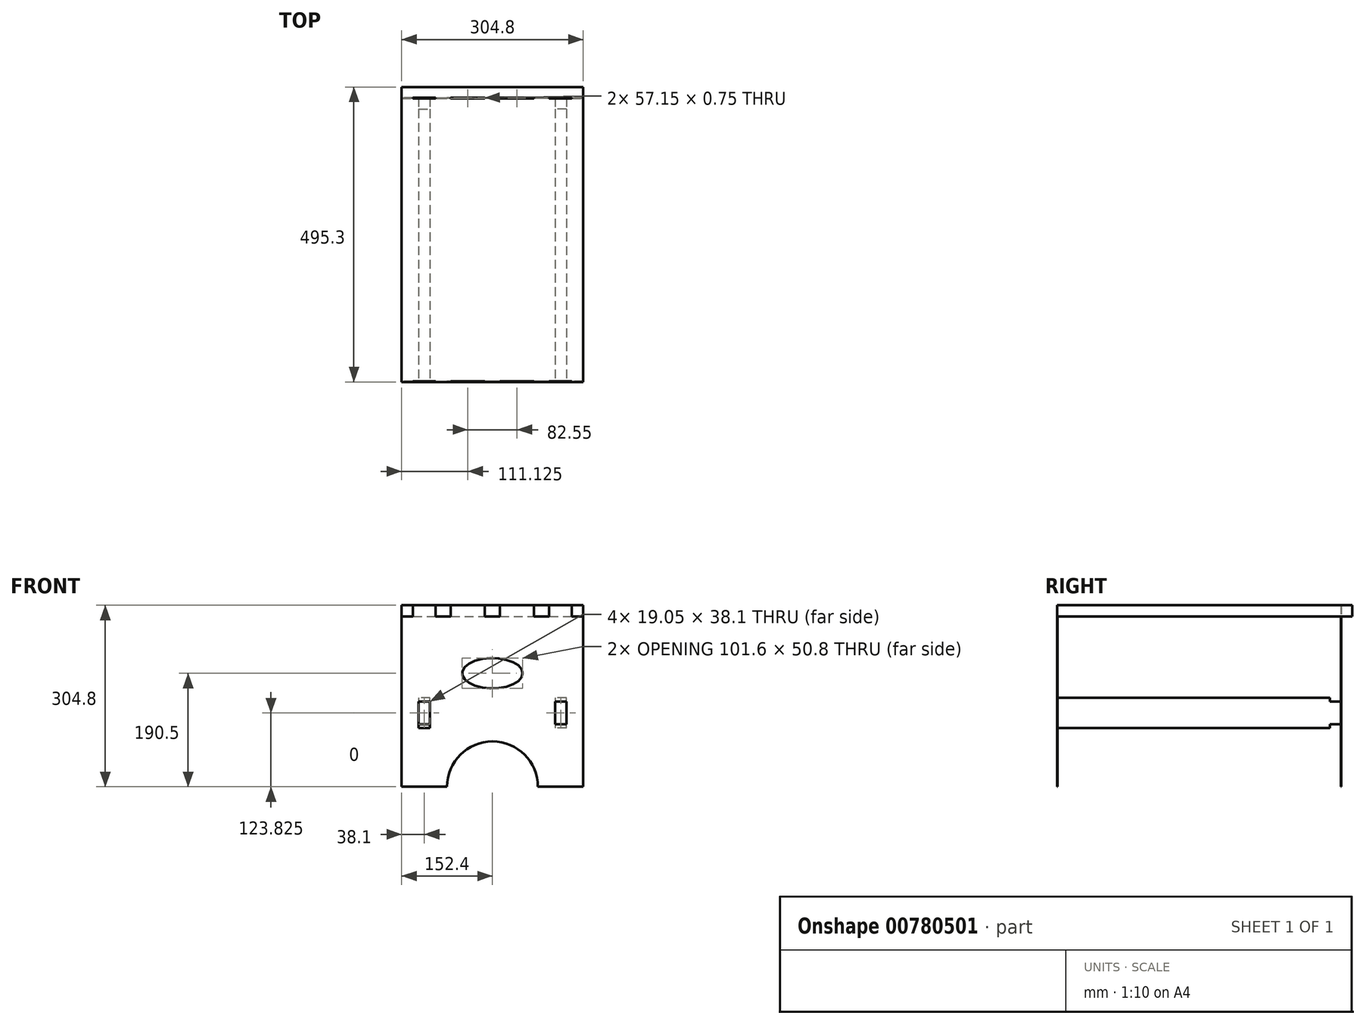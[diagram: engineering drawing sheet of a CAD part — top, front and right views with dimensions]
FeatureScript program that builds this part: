
annotation { "Feature Type Name" : "Feature", "Feature Type Description" : "" }
export const myFeature = defineFeature(function(context is Context, id is Id, definition is map)
    precondition{}
    {
        {
            assignVariable(context, id + "F0", {"name" : "PLY", "anyValue" : 0.75});
        }
        {
            var Q0;
            Q0=qCreatedBy(makeId("Front.planeOp"),FACE);
            var sketch = newSketch(context, id + "F1", { "sketchPlane" : qUnion([Q0])});
            skLineSegment(sketch, "E0", {"start": v(0, 0) * mm, "end": v(76.2, 0) * mm});
            skLineSegment(sketch, "E1", {"start": v(0, 0) * mm, "end": v(0, 304.8) * mm});
            skLineSegment(sketch, "E2", {"start": v(0, 304.8) * mm, "end": v(139.7, 304.8) * mm});
            skLineSegment(sketch, "E3", {"start": v(304.8, 304.8) * mm, "end": v(304.8, 0) * mm});
            skLineSegment(sketch, "E4", {"start": v(304.8, 0) * mm, "end": v(228.6, 0) * mm});
            skLineSegment(sketch, "E5", {"start": v(228.6, 0) * mm, "end": v(228.6, 76.2) * mm});
            skLineSegment(sketch, "E6", {"start": v(76.2, 0) * mm, "end": v(76.2, 76.2) * mm});
            skLineSegment(sketch, "E7", {"start": v(76.2, 76.2) * mm, "end": v(228.6, 76.2) * mm});
            skLineSegment(sketch, "E8", {"start": v(152.4, 304.8) * mm, "end": v(152.4, 76.2) * mm});
            skEllipse(sketch, "E9", {"center": v(152.4, 190.5) * mm, "majorRadius": 50.8 * mm, "minorRadius": 25.4 * mm, "majorAxis": v(1, 0)});
            skLineSegment(sketch, "E10", {"start": v(0, 304.8) * mm, "end": v(19.05, 304.8) * mm});
            skLineSegment(sketch, "E11", {"start": v(19.05, 304.8) * mm, "end": v(19.05, 285.75) * mm});
            skLineSegment(sketch, "E12", {"start": v(19.05, 285.75) * mm, "end": v(0, 285.75) * mm});
            skLineSegment(sketch, "E13", {"start": v(304.8, 304.8) * mm, "end": v(285.75, 304.8) * mm});
            skLineSegment(sketch, "E14", {"start": v(285.75, 304.8) * mm, "end": v(285.75, 285.75) * mm});
            skLineSegment(sketch, "E15", {"start": v(285.75, 285.75) * mm, "end": v(304.8, 285.75) * mm});
            skLineSegment(sketch, "E16", {"start": v(19.05, 304.8) * mm, "end": v(57.15, 304.8) * mm});
            skLineSegment(sketch, "E17", {"start": v(57.15, 304.8) * mm, "end": v(57.15, 285.75) * mm});
            skLineSegment(sketch, "E18", {"start": v(57.15, 285.75) * mm, "end": v(82.55, 285.75) * mm});
            skLineSegment(sketch, "E19", {"start": v(82.55, 285.75) * mm, "end": v(82.55, 304.8) * mm});
            skLineSegment(sketch, "E20", {"start": v(285.75, 304.8) * mm, "end": v(247.65, 304.8) * mm});
            skLineSegment(sketch, "E21", {"start": v(247.65, 304.8) * mm, "end": v(247.65, 285.75) * mm});
            skLineSegment(sketch, "E22", {"start": v(247.65, 285.75) * mm, "end": v(222.25, 285.75) * mm});
            skLineSegment(sketch, "E23", {"start": v(222.25, 285.75) * mm, "end": v(222.25, 304.8) * mm});
            skLineSegment(sketch, "E24", {"start": v(165.1, 304.8) * mm, "end": v(165.1, 285.75) * mm});
            skLineSegment(sketch, "E25", {"start": v(165.1, 285.75) * mm, "end": v(152.4, 285.75) * mm});
            skLineSegment(sketch, "E26", {"start": v(152.4, 285.75) * mm, "end": v(139.7, 285.75) * mm});
            skLineSegment(sketch, "E27", {"start": v(139.7, 285.75) * mm, "end": v(139.7, 304.8) * mm});
            skLineSegment(sketch, "E28.trimOffspring", {"start": v(165.1, 304.8) * mm, "end": v(304.8, 304.8) * mm});
            skLineSegment(sketch, "E29", {"start": v(266.7, 0) * mm, "end": v(266.7, 101.6) * mm});
            skLineSegment(sketch, "E30.top", {"start": v(273.94, 104.78) * mm, "end": v(261.24, 104.78) * mm});
            skLineSegment(sketch, "E30.right", {"start": v(261.24, 123.83) * mm, "end": v(261.24, 123.82) * mm});
            skLineSegment(sketch, "E31", {"start": v(266.7, 101.6) * mm, "end": v(266.7, 104.78) * mm});
            skLineSegment(sketch, "E32", {"start": v(38.1, 0) * mm, "end": v(38.1, 104.78) * mm});
            skLineSegment(sketch, "E33", {"start": v(38.1, 104.78) * mm, "end": v(44.45, 104.78) * mm});
            skLineSegment(sketch, "E34.bottom", {"start": v(38.1, 104.78) * mm, "end": v(31.75, 104.78) * mm});
            skPoint(sketch, "E35.end.orphan", {"position": v(261.24, 123.82) * mm});
            skLineSegment(sketch, "E36", {"start": v(261.24, 104.78) * mm, "end": v(258.07, 104.78) * mm});
            skLineSegment(sketch, "E37.bottom", {"start": v(276.7, 104.78) * mm, "end": v(257.64, 104.78) * mm});
            skLineSegment(sketch, "E38", {"start": v(44.45, 104.78) * mm, "end": v(47.62, 104.78) * mm});
            skLineSegment(sketch, "E39.bottom", {"start": v(47.62, 104.78) * mm, "end": v(28.57, 104.78) * mm});
            skLineSegment(sketch, "E40.top", {"start": v(47.62, 142.88) * mm, "end": v(28.57, 142.88) * mm});
            skLineSegment(sketch, "E40.left", {"start": v(47.62, 104.78) * mm, "end": v(47.62, 142.88) * mm});
            skLineSegment(sketch, "E40.right", {"start": v(28.57, 104.78) * mm, "end": v(28.57, 142.88) * mm});
            skLineSegment(sketch, "E41.top", {"start": v(276.7, 142.88) * mm, "end": v(257.64, 142.88) * mm});
            skLineSegment(sketch, "E41.left", {"start": v(276.7, 104.78) * mm, "end": v(276.7, 142.88) * mm});
            skLineSegment(sketch, "E41.right", {"start": v(257.64, 104.78) * mm, "end": v(257.64, 142.88) * mm});
            skSolve(sketch);
        }
        {
            var Q0;
            {var subQ12=sQuery(id+"F1.wireOp",EDGE,"E4");Q0=makeQuery(id+"F1.imprint","IMPRINT",FACE,{"disambiguationData":[TD([[makeQuery(id+"F1.imprint","IMPRINT",EDGE,{"derivedFrom":subQ12}),-1.0]])]});}
            var Q1;
            {var subQ10=sQuery(id+"F1.wireOp",EDGE,"E0");Q1=makeQuery(id+"F1.imprint","IMPRINT",FACE,{"disambiguationData":[TD([[makeQuery(id+"F1.imprint","IMPRINT",EDGE,{"derivedFrom":subQ10}),1.0]])]});}
            extrude(context, id + "F2", {"entities" : qUnion([Q0, Q1]), "depth" : (getVariable(context, 'PLY')) * mm, "offsetDistance" : 25.4 * mm});
        }
        {
            var Q0;
            Q0=makeQuery(id+"F2.opExtrude","SWEPT_EDGE",EDGE,{"disambiguationData":[OSD([sQuery(id+"F1.wireOp",EDGE,"E6"),sQuery(id+"F1.wireOp",EDGE,"E7")])]});
            var Q1;
            Q1=makeQuery(id+"F2.opExtrude","SWEPT_EDGE",EDGE,{"disambiguationData":[OSD([sQuery(id+"F1.wireOp",EDGE,"E5"),sQuery(id+"F1.wireOp",EDGE,"E7")])]});
            fillet(context, id + "F3", {"entities" : qUnion([Q0, Q1]), "radius" : 76.2 * mm, "tangentPropagation" : true, "allowEdgeOverflow" : false});
        }
        {
            var Q0;
            Q0=makeQuery(id+"F2.opExtrude","CAP_FACE",FACE,{"disambiguationData":[OSD([sQuery(id+"F1.wireOp",EDGE,"E0"),sQuery(id+"F1.wireOp",EDGE,"E1"),sQuery(id+"F1.wireOp",EDGE,"E2"),sQuery(id+"F1.wireOp",EDGE,"E3"),sQuery(id+"F1.wireOp",EDGE,"E4"),sQuery(id+"F1.wireOp",EDGE,"E5"),sQuery(id+"F1.wireOp",EDGE,"E6"),sQuery(id+"F1.wireOp",EDGE,"E7"),sQuery(id+"F1.wireOp",EDGE,"E9"),sQuery(id+"F1.wireOp",EDGE,"E11"),sQuery(id+"F1.wireOp",EDGE,"E12"),sQuery(id+"F1.wireOp",EDGE,"E14"),sQuery(id+"F1.wireOp",EDGE,"E15"),sQuery(id+"F1.wireOp",EDGE,"E16"),sQuery(id+"F1.wireOp",EDGE,"E17"),sQuery(id+"F1.wireOp",EDGE,"E18"),sQuery(id+"F1.wireOp",EDGE,"E19"),sQuery(id+"F1.wireOp",EDGE,"E21"),sQuery(id+"F1.wireOp",EDGE,"E22"),sQuery(id+"F1.wireOp",EDGE,"E23"),sQuery(id+"F1.wireOp",EDGE,"E24"),sQuery(id+"F1.wireOp",EDGE,"E25"),sQuery(id+"F1.wireOp",EDGE,"E26"),sQuery(id+"F1.wireOp",EDGE,"E27"),sQuery(id+"F1.wireOp",EDGE,"E28.trimOffspring"),sQuery(id+"F1.wireOp",EDGE,"E37.bottom"),sQuery(id+"F1.wireOp",EDGE,"E37.top"),sQuery(id+"F1.wireOp",EDGE,"E37.left"),sQuery(id+"F1.wireOp",EDGE,"E37.right"),sQuery(id+"F1.wireOp",EDGE,"E39.bottom"),sQuery(id+"F1.wireOp",EDGE,"E39.top"),sQuery(id+"F1.wireOp",EDGE,"E39.left"),sQuery(id+"F1.wireOp",EDGE,"E39.right")])],"isStart":true});
            var sketch = newSketch(context, id + "F4", { "sketchPlane" : qUnion([Q0])});
            skLineSegment(sketch, "E42", {"start": v(-276.7, 142.88) * mm, "end": v(-276.7, 149.23) * mm});
            skLineSegment(sketch, "E43.bottom", {"start": v(-276.7, 149.23) * mm, "end": v(-257.64, 149.23) * mm});
            skLineSegment(sketch, "E43.top", {"start": v(-276.7, 98.43) * mm, "end": v(-257.64, 98.43) * mm});
            skLineSegment(sketch, "E43.left", {"start": v(-276.7, 149.23) * mm, "end": v(-276.7, 98.43) * mm});
            skLineSegment(sketch, "E43.right", {"start": v(-257.64, 149.23) * mm, "end": v(-257.64, 98.43) * mm});
            skLineSegment(sketch, "E44", {"start": v(-47.62, 142.88) * mm, "end": v(-47.62, 149.22) * mm});
            skLineSegment(sketch, "E45.bottom", {"start": v(-47.62, 149.22) * mm, "end": v(-28.57, 149.22) * mm});
            skLineSegment(sketch, "E45.top", {"start": v(-47.62, 98.42) * mm, "end": v(-28.57, 98.42) * mm});
            skLineSegment(sketch, "E45.left", {"start": v(-47.62, 149.22) * mm, "end": v(-47.62, 98.42) * mm});
            skLineSegment(sketch, "E45.right", {"start": v(-28.57, 149.22) * mm, "end": v(-28.57, 98.42) * mm});
            skSolve(sketch);
        }
        {
            var Q0;
            Q0=makeQuery(id+"F2.opExtrude","CAP_FACE",FACE,{"disambiguationData":[OSD([sQuery(id+"F1.wireOp",EDGE,"E0"),sQuery(id+"F1.wireOp",EDGE,"E1"),sQuery(id+"F1.wireOp",EDGE,"E2"),sQuery(id+"F1.wireOp",EDGE,"E3"),sQuery(id+"F1.wireOp",EDGE,"E4"),sQuery(id+"F1.wireOp",EDGE,"E5"),sQuery(id+"F1.wireOp",EDGE,"E6"),sQuery(id+"F1.wireOp",EDGE,"E7"),sQuery(id+"F1.wireOp",EDGE,"E9"),sQuery(id+"F1.wireOp",EDGE,"E11"),sQuery(id+"F1.wireOp",EDGE,"E12"),sQuery(id+"F1.wireOp",EDGE,"E14"),sQuery(id+"F1.wireOp",EDGE,"E15"),sQuery(id+"F1.wireOp",EDGE,"E16"),sQuery(id+"F1.wireOp",EDGE,"E17"),sQuery(id+"F1.wireOp",EDGE,"E18"),sQuery(id+"F1.wireOp",EDGE,"E19"),sQuery(id+"F1.wireOp",EDGE,"E21"),sQuery(id+"F1.wireOp",EDGE,"E22"),sQuery(id+"F1.wireOp",EDGE,"E23"),sQuery(id+"F1.wireOp",EDGE,"E24"),sQuery(id+"F1.wireOp",EDGE,"E25"),sQuery(id+"F1.wireOp",EDGE,"E26"),sQuery(id+"F1.wireOp",EDGE,"E27"),sQuery(id+"F1.wireOp",EDGE,"E28.trimOffspring"),sQuery(id+"F1.wireOp",EDGE,"E37.bottom"),sQuery(id+"F1.wireOp",EDGE,"E37.top"),sQuery(id+"F1.wireOp",EDGE,"E37.left"),sQuery(id+"F1.wireOp",EDGE,"E37.right"),sQuery(id+"F1.wireOp",EDGE,"E39.bottom"),sQuery(id+"F1.wireOp",EDGE,"E39.top"),sQuery(id+"F1.wireOp",EDGE,"E39.left"),sQuery(id+"F1.wireOp",EDGE,"E39.right")])],"isStart":false});
            var sketch = newSketch(context, id + "F5", { "sketchPlane" : qUnion([Q0])});
            skLineSegment(sketch, "E46", {"start": v(0, 285.75) * mm, "end": v(0, 304.8) * mm});
            skLineSegment(sketch, "E47.bottom", {"start": v(0, 304.8) * mm, "end": v(304.8, 304.8) * mm});
            skLineSegment(sketch, "E47.top", {"start": v(0, 285.75) * mm, "end": v(304.8, 285.75) * mm});
            skLineSegment(sketch, "E47.left", {"start": v(0, 304.8) * mm, "end": v(0, 285.75) * mm});
            skLineSegment(sketch, "E47.right", {"start": v(304.8, 304.8) * mm, "end": v(304.8, 285.75) * mm});
            skSolve(sketch);
        }
        {
            var Q0;
            Q0 = qSketchRegion(id + "F5", true);
            extrude(context, id + "F6", {"entities" : qUnion([Q0]), "oppositeDirection" : true, "depth" : 495.3 * mm, "offsetDistance" : 25.4 * mm});
        }
        {
            var Q0;
            Q0=makeQuery(id+"F2.opExtrude","SWEPT_BODY",BODY,{"disambiguationData":[OSD([sQuery(id+"F1.wireOp",EDGE,"E0"),sQuery(id+"F1.wireOp",EDGE,"E1"),sQuery(id+"F1.wireOp",EDGE,"E2"),sQuery(id+"F1.wireOp",EDGE,"E3"),sQuery(id+"F1.wireOp",EDGE,"E4"),sQuery(id+"F1.wireOp",EDGE,"E5"),sQuery(id+"F1.wireOp",EDGE,"E6"),sQuery(id+"F1.wireOp",EDGE,"E7"),sQuery(id+"F1.wireOp",EDGE,"E9"),sQuery(id+"F1.wireOp",EDGE,"E11"),sQuery(id+"F1.wireOp",EDGE,"E12"),sQuery(id+"F1.wireOp",EDGE,"E14"),sQuery(id+"F1.wireOp",EDGE,"E15"),sQuery(id+"F1.wireOp",EDGE,"E16"),sQuery(id+"F1.wireOp",EDGE,"E17"),sQuery(id+"F1.wireOp",EDGE,"E18"),sQuery(id+"F1.wireOp",EDGE,"E19"),sQuery(id+"F1.wireOp",EDGE,"E21"),sQuery(id+"F1.wireOp",EDGE,"E22"),sQuery(id+"F1.wireOp",EDGE,"E23"),sQuery(id+"F1.wireOp",EDGE,"E24"),sQuery(id+"F1.wireOp",EDGE,"E25"),sQuery(id+"F1.wireOp",EDGE,"E26"),sQuery(id+"F1.wireOp",EDGE,"E27"),sQuery(id+"F1.wireOp",EDGE,"E28.trimOffspring"),sQuery(id+"F1.wireOp",EDGE,"E39.bottom"),sQuery(id+"F1.wireOp",EDGE,"E40.top"),sQuery(id+"F1.wireOp",EDGE,"E40.left"),sQuery(id+"F1.wireOp",EDGE,"E40.right"),sQuery(id+"F1.wireOp",EDGE,"E37.bottom"),sQuery(id+"F1.wireOp",EDGE,"E41.top"),sQuery(id+"F1.wireOp",EDGE,"E41.left"),sQuery(id+"F1.wireOp",EDGE,"E41.right")])]});
            var Q1;
            Q1=makeQuery(id+"F6.opExtrude","SWEPT_BODY",BODY,{"disambiguationData":[OSD([sQuery(id+"F5.wireOp",EDGE,"E47.bottom"),sQuery(id+"F5.wireOp",EDGE,"E47.top"),sQuery(id+"F5.wireOp",EDGE,"E47.left"),sQuery(id+"F5.wireOp",EDGE,"E47.right")])]});
            booleanBodies(context, id + "F7", {"operationType" : BooleanOperationType.SUBTRACTION, "tools" : qUnion([Q0]), "targets" : qUnion([Q1]), "keepTools" : true});
        }
        {
            var Q0;
            Q0 = qSketchRegion(id + "F4", true);
            extrude(context, id + "F8", {"entities" : qUnion([Q0]), "depth" : 457.2 * mm, "offsetDistance" : 25.4 * mm});
        }
        {
            var Q0;
            {var subQ1=makeQuery(id+"F2.opExtrude","CAP_EDGE",EDGE,{"disambiguationData":[OSD([sQuery(id+"F1.wireOp",EDGE,"E37.bottom")])],"isStart":true});Q0=makeQuery(id+"F4.imprint","IMPRINT",FACE,{"disambiguationData":[TD([[makeQuery(id+"F4.imprint","IMPRINT",EDGE,{"derivedFrom":subQ1}),1.0]])]});}
            var Q1;
            {var subQ1=makeQuery(id+"F2.opExtrude","CAP_EDGE",EDGE,{"disambiguationData":[OSD([sQuery(id+"F1.wireOp",EDGE,"E39.bottom")])],"isStart":true});Q1=makeQuery(id+"F4.imprint","IMPRINT",FACE,{"disambiguationData":[TD([[makeQuery(id+"F4.imprint","IMPRINT",EDGE,{"derivedFrom":subQ1}),1.0]])]});}
            extrude(context, id + "F9", {"entities" : qUnion([Q0, Q1]), "oppositeDirection" : true, "depth" : (getVariable(context, 'PLY')) * mm, "offsetDistance" : 25.4 * mm});
        }
        {
            var Q0;
            Q0=makeQuery(id+"F8.opExtrude","CAP_FACE",FACE,{"disambiguationData":[OSD([sQuery(id+"F4.wireOp",EDGE,"E43.bottom"),sQuery(id+"F4.wireOp",EDGE,"E43.top"),sQuery(id+"F4.wireOp",EDGE,"E43.left"),sQuery(id+"F4.wireOp",EDGE,"E43.right")])],"isStart":false});
            var sketch = newSketch(context, id + "F10", { "sketchPlane" : qUnion([Q0])});
            skLineSegment(sketch, "E48.bottom", {"start": v(-276.7, 142.88) * mm, "end": v(-257.64, 142.88) * mm});
            skLineSegment(sketch, "E48.top", {"start": v(-276.7, 104.78) * mm, "end": v(-257.64, 104.78) * mm});
            skLineSegment(sketch, "E48.left", {"start": v(-276.7, 142.88) * mm, "end": v(-276.7, 104.78) * mm});
            skLineSegment(sketch, "E48.right", {"start": v(-257.64, 142.88) * mm, "end": v(-257.64, 104.78) * mm});
            skSolve(sketch);
        }
        {
            var Q0;
            Q0 = qSketchRegion(id + "F10", true);
            extrude(context, id + "F11", {"entities" : qUnion([Q0]), "operationType" : NewBodyOperationType.ADD, "depth" : 19.05 * mm, "offsetDistance" : 25.4 * mm});
        }
        {
            var Q0;
            Q0=makeQuery(id+"F8.opExtrude","CAP_FACE",FACE,{"disambiguationData":[OSD([sQuery(id+"F4.wireOp",EDGE,"E45.bottom"),sQuery(id+"F4.wireOp",EDGE,"E45.top"),sQuery(id+"F4.wireOp",EDGE,"E45.left"),sQuery(id+"F4.wireOp",EDGE,"E45.right")])],"isStart":false});
            var sketch = newSketch(context, id + "F12", { "sketchPlane" : qUnion([Q0])});
            skLineSegment(sketch, "E49", {"start": v(-28.57, 149.22) * mm, "end": v(-28.57, 142.88) * mm});
            skLineSegment(sketch, "E50.bottom", {"start": v(-28.57, 142.88) * mm, "end": v(-47.62, 142.88) * mm});
            skLineSegment(sketch, "E50.top", {"start": v(-28.57, 104.78) * mm, "end": v(-47.62, 104.78) * mm});
            skLineSegment(sketch, "E50.left", {"start": v(-28.57, 142.88) * mm, "end": v(-28.57, 104.78) * mm});
            skLineSegment(sketch, "E50.right", {"start": v(-47.62, 142.88) * mm, "end": v(-47.62, 104.78) * mm});
            skSolve(sketch);
        }
        {
            var Q0;
            Q0 = qSketchRegion(id + "F12", true);
            extrude(context, id + "F13", {"entities" : qUnion([Q0]), "operationType" : NewBodyOperationType.ADD, "depth" : 19.05 * mm, "offsetDistance" : 25.4 * mm});
        }
        {
            var Q0;
            Q0=makeQuery(id+"F2.opExtrude","SWEPT_BODY",BODY,{"disambiguationData":[OSD([sQuery(id+"F1.wireOp",EDGE,"E0"),sQuery(id+"F1.wireOp",EDGE,"E1"),sQuery(id+"F1.wireOp",EDGE,"E2"),sQuery(id+"F1.wireOp",EDGE,"E3"),sQuery(id+"F1.wireOp",EDGE,"E4"),sQuery(id+"F1.wireOp",EDGE,"E5"),sQuery(id+"F1.wireOp",EDGE,"E6"),sQuery(id+"F1.wireOp",EDGE,"E7"),sQuery(id+"F1.wireOp",EDGE,"E9"),sQuery(id+"F1.wireOp",EDGE,"E11"),sQuery(id+"F1.wireOp",EDGE,"E12"),sQuery(id+"F1.wireOp",EDGE,"E14"),sQuery(id+"F1.wireOp",EDGE,"E15"),sQuery(id+"F1.wireOp",EDGE,"E16"),sQuery(id+"F1.wireOp",EDGE,"E17"),sQuery(id+"F1.wireOp",EDGE,"E18"),sQuery(id+"F1.wireOp",EDGE,"E19"),sQuery(id+"F1.wireOp",EDGE,"E21"),sQuery(id+"F1.wireOp",EDGE,"E22"),sQuery(id+"F1.wireOp",EDGE,"E23"),sQuery(id+"F1.wireOp",EDGE,"E24"),sQuery(id+"F1.wireOp",EDGE,"E25"),sQuery(id+"F1.wireOp",EDGE,"E26"),sQuery(id+"F1.wireOp",EDGE,"E27"),sQuery(id+"F1.wireOp",EDGE,"E28.trimOffspring"),sQuery(id+"F1.wireOp",EDGE,"E39.bottom"),sQuery(id+"F1.wireOp",EDGE,"E40.top"),sQuery(id+"F1.wireOp",EDGE,"E40.left"),sQuery(id+"F1.wireOp",EDGE,"E40.right"),sQuery(id+"F1.wireOp",EDGE,"E37.bottom"),sQuery(id+"F1.wireOp",EDGE,"E41.top"),sQuery(id+"F1.wireOp",EDGE,"E41.left"),sQuery(id+"F1.wireOp",EDGE,"E41.right")])]});
            var Q1;
            Q1=makeQuery(id+"F13.opExtrude","CAP_FACE",FACE,{"disambiguationData":[OSD([sQuery(id+"F12.wireOp",EDGE,"E50.bottom"),sQuery(id+"F12.wireOp",EDGE,"E50.top"),sQuery(id+"F12.wireOp",EDGE,"E50.left"),sQuery(id+"F12.wireOp",EDGE,"E50.right")])],"isStart":false});
            transform(context, id + "F14", {"entities" : qUnion([Q0]), "transformType" : TransformType.TRANSLATION_DISTANCE, "transformDirection" : qUnion([Q1]), "distance" : 476.25 * mm, "makeCopy" : true});
        }
        {
            var Q0;
            Q0=makeQuery(id+"F14.opPattern","COPY",BODY,{"derivedFrom":makeQuery(id+"F2.opExtrude","SWEPT_BODY",BODY,{"disambiguationData":[OSD([sQuery(id+"F1.wireOp",EDGE,"E0"),sQuery(id+"F1.wireOp",EDGE,"E1"),sQuery(id+"F1.wireOp",EDGE,"E2"),sQuery(id+"F1.wireOp",EDGE,"E3"),sQuery(id+"F1.wireOp",EDGE,"E4"),sQuery(id+"F1.wireOp",EDGE,"E5"),sQuery(id+"F1.wireOp",EDGE,"E6"),sQuery(id+"F1.wireOp",EDGE,"E7"),sQuery(id+"F1.wireOp",EDGE,"E9"),sQuery(id+"F1.wireOp",EDGE,"E11"),sQuery(id+"F1.wireOp",EDGE,"E12"),sQuery(id+"F1.wireOp",EDGE,"E14"),sQuery(id+"F1.wireOp",EDGE,"E15"),sQuery(id+"F1.wireOp",EDGE,"E16"),sQuery(id+"F1.wireOp",EDGE,"E17"),sQuery(id+"F1.wireOp",EDGE,"E18"),sQuery(id+"F1.wireOp",EDGE,"E19"),sQuery(id+"F1.wireOp",EDGE,"E21"),sQuery(id+"F1.wireOp",EDGE,"E22"),sQuery(id+"F1.wireOp",EDGE,"E23"),sQuery(id+"F1.wireOp",EDGE,"E24"),sQuery(id+"F1.wireOp",EDGE,"E25"),sQuery(id+"F1.wireOp",EDGE,"E26"),sQuery(id+"F1.wireOp",EDGE,"E27"),sQuery(id+"F1.wireOp",EDGE,"E28.trimOffspring"),sQuery(id+"F1.wireOp",EDGE,"E39.bottom"),sQuery(id+"F1.wireOp",EDGE,"E40.top"),sQuery(id+"F1.wireOp",EDGE,"E40.left"),sQuery(id+"F1.wireOp",EDGE,"E40.right"),sQuery(id+"F1.wireOp",EDGE,"E37.bottom"),sQuery(id+"F1.wireOp",EDGE,"E41.top"),sQuery(id+"F1.wireOp",EDGE,"E41.left"),sQuery(id+"F1.wireOp",EDGE,"E41.right")])]}),"instanceName":"1"});
            var Q1;
            Q1=makeQuery(id+"F6.opExtrude","SWEPT_BODY",BODY,{"disambiguationData":[OSD([sQuery(id+"F5.wireOp",EDGE,"E47.bottom"),sQuery(id+"F5.wireOp",EDGE,"E47.top"),sQuery(id+"F5.wireOp",EDGE,"E47.left"),sQuery(id+"F5.wireOp",EDGE,"E47.right")])]});
            booleanBodies(context, id + "F15", {"operationType" : BooleanOperationType.SUBTRACTION, "tools" : qUnion([Q0]), "targets" : qUnion([Q1]), "keepTools" : true});
        }
    });
